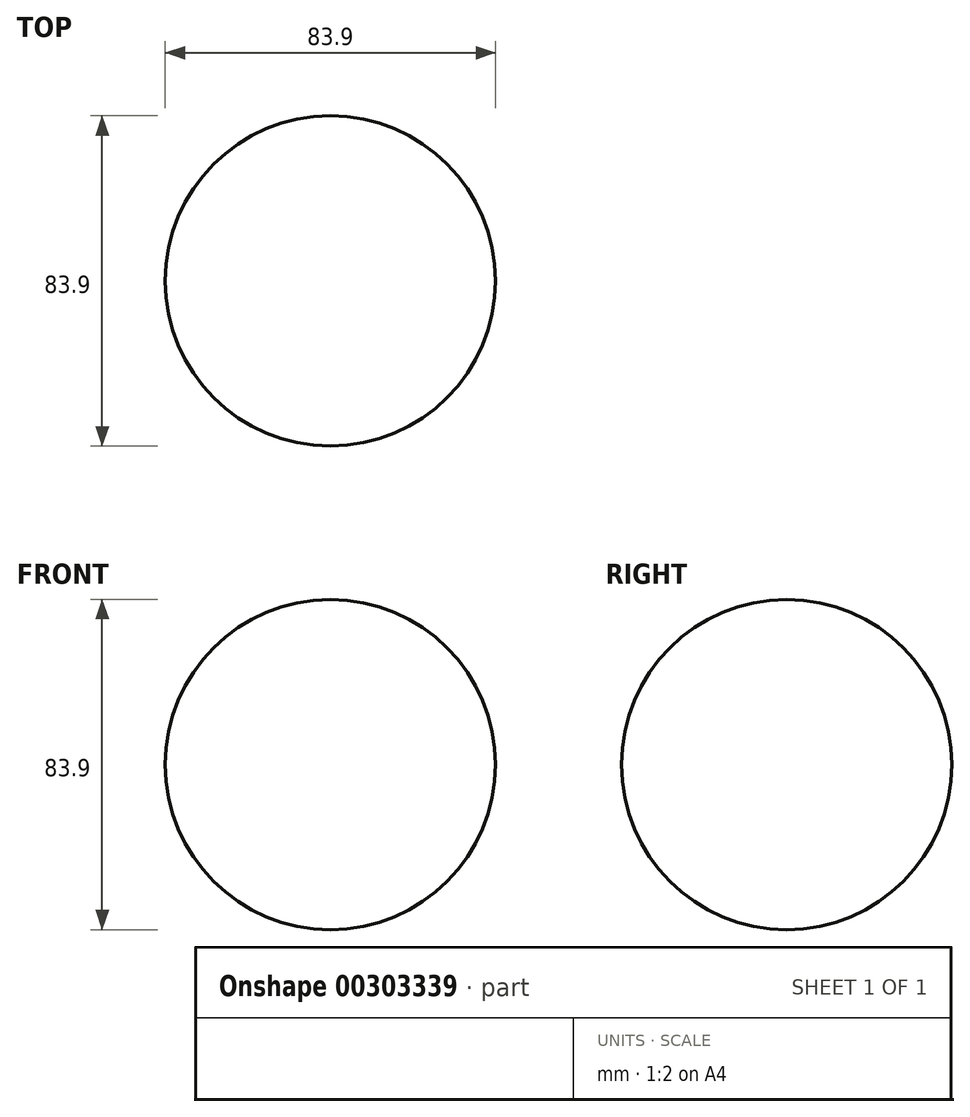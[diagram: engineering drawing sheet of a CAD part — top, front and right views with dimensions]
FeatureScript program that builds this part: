
annotation { "Feature Type Name" : "Feature", "Feature Type Description" : "" }
export const myFeature = defineFeature(function(context is Context, id is Id, definition is map)
    precondition{}
    {
        {
            var Q0;
            Q0=qCreatedBy(makeId("Front.planeOp"),FACE);
            var sketch = newSketch(context, id + "F0", { "sketchPlane" : qUnion([Q0])});
            skArc(sketch, "E0", {"start": v(0, -41.95) * mm, "mid": v(41.95, 0) * mm, "end": v(0, 41.95) * mm});
            skLineSegment(sketch, "E1", {"start": v(0, 0) * mm, "end": v(0, 41.95) * mm});
            skLineSegment(sketch, "E2", {"start": v(0, 0) * mm, "end": v(0, -41.95) * mm});
            skSolve(sketch);
        }
        {
            var Q0;
            Q0=makeQuery(id+"F0.imprint","IMPRINT",FACE,{"disambiguationData":[TD([[makeQuery(id+"F0.imprint","IMPRINT",EDGE,{"derivedFrom":sQuery(id+"F0.wireOp",EDGE,"E0")}),1.0]])]});
            var Q1;
            Q1=sQuery(id+"F0.wireOp",EDGE,"E1");
            revolve(context, id + "F1", {"entities" : qUnion([Q0]), "axis" : qUnion([Q1]), "revolveType" : RevolveType.FULL});
        }
    });
